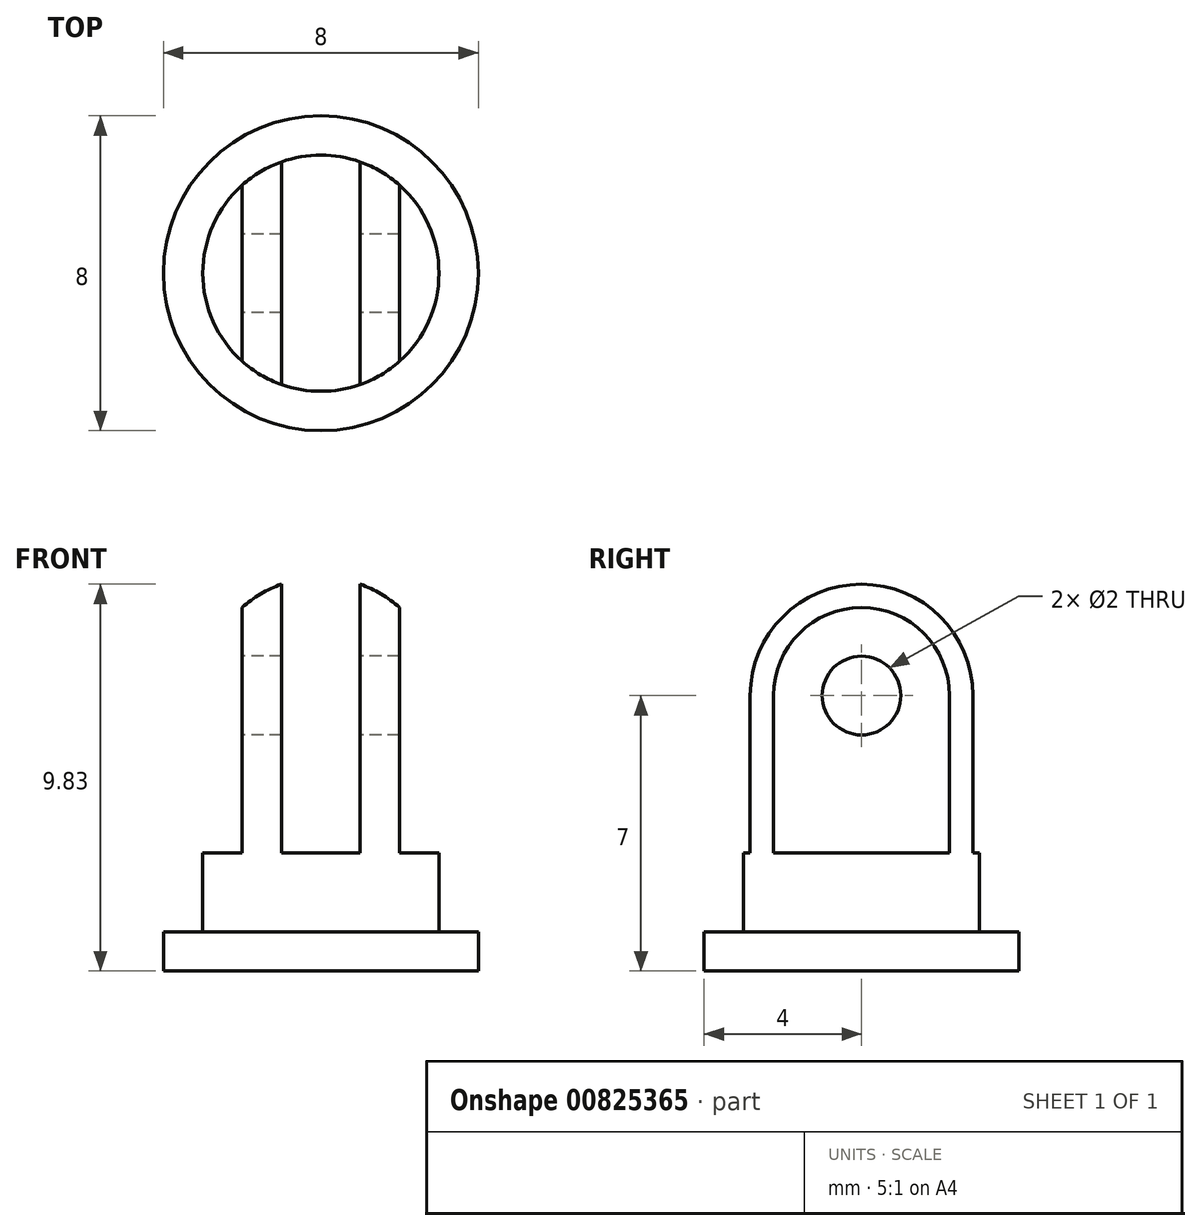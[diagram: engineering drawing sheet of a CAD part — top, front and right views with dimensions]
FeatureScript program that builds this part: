
annotation { "Feature Type Name" : "Feature", "Feature Type Description" : "" }
export const myFeature = defineFeature(function(context is Context, id is Id, definition is map)
    precondition{}
    {
        {
            var Q0;
            Q0=qCreatedBy(makeId("Top.planeOp"),FACE);
            var sketch = newSketch(context, id + "F0", { "sketchPlane" : qUnion([Q0])});
            skCircle(sketch, "E0", {"center": v(0, 0) * mm, "radius": 4 * mm});
            skSolve(sketch);
        }
        {
            var Q0;
            Q0 = qSketchRegion(id + "F0", true);
            extrude(context, id + "F1", {"entities" : qUnion([Q0]), "depth" : 1 * mm, "offsetDistance" : 25 * mm});
        }
        {
            var Q0;
            Q0=makeQuery(id+"F1.opExtrude","CAP_FACE",FACE,{"disambiguationData":[OSD([sQuery(id+"F0.wireOp",EDGE,"E0")])],"isStart":false});
            var sketch = newSketch(context, id + "F2", { "sketchPlane" : qUnion([Q0])});
            skCircle(sketch, "E1", {"center": v(0, 0) * mm, "radius": 3 * mm});
            skSolve(sketch);
        }
        {
            var Q0;
            Q0 = qSketchRegion(id + "F2", true);
            extrude(context, id + "F3", {"entities" : qUnion([Q0]), "operationType" : NewBodyOperationType.ADD, "depth" : 9 * mm, "offsetDistance" : 25 * mm});
        }
        {
            var Q0;
            Q0=makeQuery(id+"F3.opExtrude","CAP_FACE",FACE,{"disambiguationData":[OSD([sQuery(id+"F2.wireOp",EDGE,"E1")])],"isStart":false});
            fillet(context, id + "F4", {"entities" : qUnion([Q0]), "radius" : 3 * mm, "tangentPropagation" : true, "allowEdgeOverflow" : false});
        }
        {
            var Q0;
            Q0=qCreatedBy(makeId("Front.planeOp"),FACE);
            var sketch = newSketch(context, id + "F5", { "sketchPlane" : qUnion([Q0])});
            skLineSegment(sketch, "E2", {"start": v(0, 0) * mm, "end": v(0, 3) * mm, "construction": true});
            skLineSegment(sketch, "E3", {"start": v(0, 3) * mm, "end": v(1, 3) * mm});
            skLineSegment(sketch, "E4", {"start": v(0, 3) * mm, "end": v(-1, 3) * mm});
            skLineSegment(sketch, "E5", {"start": v(1, 3) * mm, "end": v(1, 10.66) * mm});
            skLineSegment(sketch, "E6", {"start": v(-1, 3) * mm, "end": v(-1, 10.66) * mm});
            skLineSegment(sketch, "E7", {"start": v(-1, 10.66) * mm, "end": v(1, 10.66) * mm});
            skLineSegment(sketch, "E8", {"start": v(1, 3) * mm, "end": v(2, 3) * mm, "construction": true});
            skLineSegment(sketch, "E9", {"start": v(-1, 3) * mm, "end": v(-2, 3) * mm, "construction": true});
            skLineSegment(sketch, "E10.bottom", {"start": v(2, 3) * mm, "end": v(3.55, 3) * mm});
            skLineSegment(sketch, "E10.top", {"start": v(2, 10.63) * mm, "end": v(3.55, 10.63) * mm});
            skLineSegment(sketch, "E10.left", {"start": v(2, 3) * mm, "end": v(2, 10.63) * mm});
            skLineSegment(sketch, "E10.right", {"start": v(3.55, 3) * mm, "end": v(3.55, 10.63) * mm});
            skLineSegment(sketch, "E11.bottom", {"start": v(-2, 3) * mm, "end": v(-3.65, 3) * mm});
            skLineSegment(sketch, "E11.top", {"start": v(-2, 10.7) * mm, "end": v(-3.65, 10.7) * mm});
            skLineSegment(sketch, "E11.left", {"start": v(-2, 3) * mm, "end": v(-2, 10.7) * mm});
            skLineSegment(sketch, "E11.right", {"start": v(-3.65, 3) * mm, "end": v(-3.65, 10.7) * mm});
            skSolve(sketch);
        }
        {
            var Q0;
            Q0 = qSketchRegion(id + "F5", true);
            extrude(context, id + "F6", {"entities" : qUnion([Q0]), "operationType" : NewBodyOperationType.REMOVE, "endBound" : BoundingType.SYMMETRIC, "oppositeDirection" : true, "depth" : 11 * mm, "offsetDistance" : 25 * mm});
        }
        {
            var Q0;
            Q0=makeQuery(id+"F6.boolean.opBoolean","COPY",FACE,{"derivedFrom":makeQuery(id+"F6.opExtrude","SWEPT_FACE",FACE,{"disambiguationData":[OSD([sQuery(id+"F5.wireOp",EDGE,"E11.left")])]})});
            var sketch = newSketch(context, id + "F7", { "sketchPlane" : qUnion([Q0])});
            skLineSegment(sketch, "E12", {"start": v(0, 0) * mm, "end": v(0, 7) * mm, "construction": true});
            skCircle(sketch, "E13", {"center": v(0, 7) * mm, "radius": 1 * mm});
            skSolve(sketch);
        }
        {
            var Q0;
            Q0 = qSketchRegion(id + "F7", true);
            extrude(context, id + "F8", {"entities" : qUnion([Q0]), "operationType" : NewBodyOperationType.REMOVE, "oppositeDirection" : true, "depth" : 25 * mm, "offsetDistance" : 25 * mm});
        }
    });
